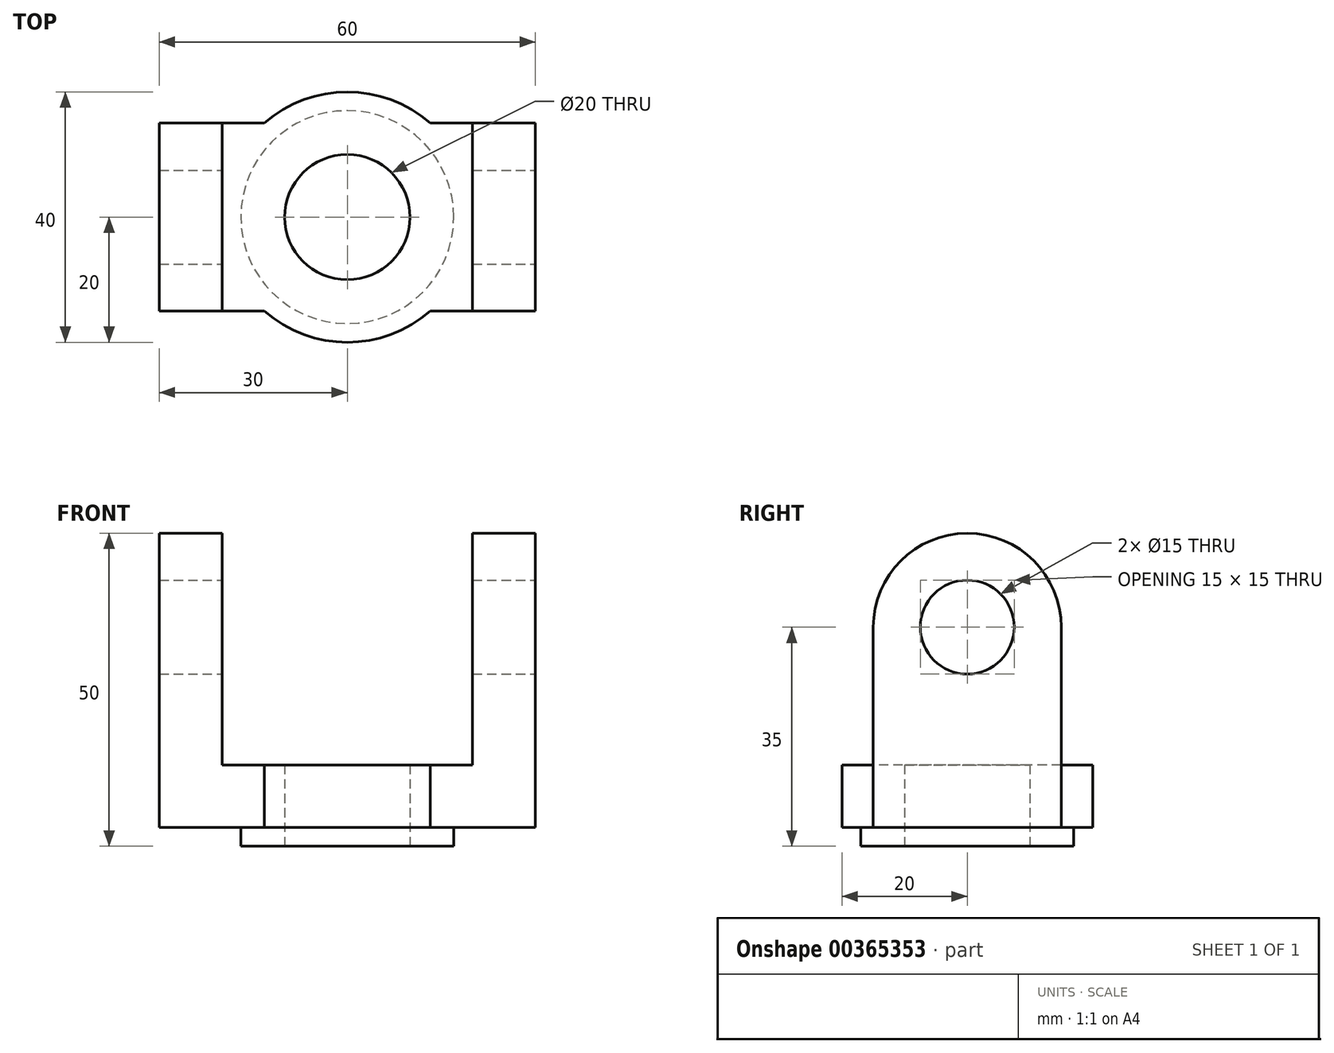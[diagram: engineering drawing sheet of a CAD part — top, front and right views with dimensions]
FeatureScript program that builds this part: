
annotation { "Feature Type Name" : "Feature", "Feature Type Description" : "" }
export const myFeature = defineFeature(function(context is Context, id is Id, definition is map)
    precondition{}
    {
        {
            var Q0;
            Q0=qCreatedBy(makeId("Top.planeOp"),FACE);
            var sketch = newSketch(context, id + "F0", { "sketchPlane" : qUnion([Q0])});
            skArc(sketch, "E0", {"start": v(-13.23, -15) * mm, "mid": v(0, -20) * mm, "end": v(13.23, -15) * mm});
            skLineSegment(sketch, "E1.bottom", {"start": v(-30, 15) * mm, "end": v(30, 15) * mm});
            skLineSegment(sketch, "E1.top", {"start": v(-30, -15) * mm, "end": v(30, -15) * mm});
            skLineSegment(sketch, "E1.left", {"start": v(-30, 15) * mm, "end": v(-30, -15) * mm});
            skLineSegment(sketch, "E1.right", {"start": v(30, 15) * mm, "end": v(30, -15) * mm});
            skCircle(sketch, "E2", {"center": v(0, 0) * mm, "radius": 10 * mm});
            skArc(sketch, "E3.trimOffspring", {"start": v(13.23, 15) * mm, "mid": v(0, 20) * mm, "end": v(-13.23, 15) * mm});
            skSolve(sketch);
        }
        {
            var Q0;
            {var subQ0=sQuery(id+"F0.wireOp",EDGE,"E3.trimOffspring");Q0=makeQuery(id+"F0.imprint","IMPRINT",FACE,{"disambiguationData":[TD([[makeQuery(id+"F0.imprint","IMPRINT",EDGE,{"derivedFrom":subQ0}),1.0]])]});}
            var Q1;
            {var subQ3=sQuery(id+"F0.wireOp",EDGE,"E1.left");Q1=makeQuery(id+"F0.imprint","IMPRINT",FACE,{"disambiguationData":[TD([[makeQuery(id+"F0.imprint","IMPRINT",EDGE,{"derivedFrom":subQ3}),1.0]])]});}
            var Q2;
            {var subQ0=sQuery(id+"F0.wireOp",EDGE,"E0");Q2=makeQuery(id+"F0.imprint","IMPRINT",FACE,{"disambiguationData":[TD([[makeQuery(id+"F0.imprint","IMPRINT",EDGE,{"derivedFrom":subQ0}),1.0]])]});}
            extrude(context, id + "F1", {"entities" : qUnion([Q0, Q1, Q2]), "depth" : 50 * mm});
        }
        {
            var Q0;
            Q0=qCreatedBy(makeId("Front.planeOp"),FACE);
            var sketch = newSketch(context, id + "F2", { "sketchPlane" : qUnion([Q0])});
            skLineSegment(sketch, "E4", {"start": v(17, 0) * mm, "end": v(17, 3) * mm});
            skLineSegment(sketch, "E5", {"start": v(17, 3) * mm, "end": v(30, 3) * mm});
            skLineSegment(sketch, "E6", {"start": v(20, 50) * mm, "end": v(20, 13) * mm});
            skLineSegment(sketch, "E7", {"start": v(-17, 3) * mm, "end": v(-17, 0) * mm});
            skLineSegment(sketch, "E8", {"start": v(-17, 3) * mm, "end": v(-30, 3) * mm});
            skLineSegment(sketch, "E9", {"start": v(-20, 50) * mm, "end": v(-20, 13) * mm});
            skLineSegment(sketch, "E10", {"start": v(-20, 13) * mm, "end": v(20, 13) * mm});
            skLineSegment(sketch, "E11", {"start": v(-20, 50) * mm, "end": v(20, 50) * mm});
            skLineSegment(sketch, "E12", {"start": v(-30, 3) * mm, "end": v(-30, 0) * mm});
            skLineSegment(sketch, "E13", {"start": v(-30, 0) * mm, "end": v(-17, 0) * mm});
            skLineSegment(sketch, "E14", {"start": v(17, 0) * mm, "end": v(30, 0) * mm});
            skLineSegment(sketch, "E15", {"start": v(30, 0) * mm, "end": v(30, 3) * mm});
            skPoint(sketch, "E16.end.orphan", {"position": v(-30, 50) * mm});
            skLineSegment(sketch, "E17", {"start": v(0, 50) * mm, "end": v(0, 13) * mm, "construction": true});
            skSolve(sketch);
        }
        {
            var Q0;
            Q0 = qSketchRegion(id + "F2", true);
            extrude(context, id + "F3", {"entities" : qUnion([Q0]), "operationType" : NewBodyOperationType.REMOVE, "endBound" : BoundingType.SYMMETRIC, "oppositeDirection" : true, "depth" : 75 * mm});
        }
        {
            var Q0;
            Q0=makeQuery(id+"F1.opExtrude","CAP_FACE",FACE,{"disambiguationData":[OSD([sQuery(id+"F0.wireOp",EDGE,"E0"),sQuery(id+"F0.wireOp",EDGE,"E1.bottom"),sQuery(id+"F0.wireOp",EDGE,"E1.top"),sQuery(id+"F0.wireOp",EDGE,"E1.left"),sQuery(id+"F0.wireOp",EDGE,"E1.right"),sQuery(id+"F0.wireOp",EDGE,"E2"),sQuery(id+"F0.wireOp",EDGE,"E3.trimOffspring")])],"isStart":true});
            var sketch = newSketch(context, id + "F4", { "sketchPlane" : qUnion([Q0])});
            skCircle(sketch, "E18", {"center": v(0, 0) * mm, "radius": 17 * mm});
            skSolve(sketch);
        }
        {
            var Q0;
            {var subQ1=sQuery(id+"F0.wireOp",EDGE,"E0");Q0=makeQuery(id+"F4.imprint","IMPRINT",FACE,{"disambiguationData":[TD([[makeQuery(id+"F4.imprint","IMPRINT",EDGE,{"derivedFrom":makeQuery(id+"F1.opExtrude","CAP_EDGE",EDGE,{"disambiguationData":[OSD([subQ1])],"isStart":true})}),-1.0]])]});}
            var Q1;
            {var subQ1=sQuery(id+"F0.wireOp",EDGE,"E3.trimOffspring");Q1=makeQuery(id+"F4.imprint","IMPRINT",FACE,{"disambiguationData":[TD([[makeQuery(id+"F4.imprint","IMPRINT",EDGE,{"derivedFrom":makeQuery(id+"F1.opExtrude","CAP_EDGE",EDGE,{"disambiguationData":[OSD([subQ1])],"isStart":true})}),-1.0]])]});}
            extrude(context, id + "F5", {"entities" : qUnion([Q0, Q1]), "operationType" : NewBodyOperationType.REMOVE, "oppositeDirection" : true, "depth" : 3 * mm});
        }
        {
            var Q0;
            Q0=makeQuery(id+"F1.opExtrude","SWEPT_FACE",FACE,{"disambiguationData":[OSD([sQuery(id+"F0.wireOp",EDGE,"E1.right")])]});
            var sketch = newSketch(context, id + "F6", { "sketchPlane" : qUnion([Q0])});
            skLineSegment(sketch, "E19", {"start": v(0, 3) * mm, "end": v(0, 35) * mm, "construction": true});
            skCircle(sketch, "E20", {"center": v(0, 35) * mm, "radius": 7.5 * mm});
            skCircle(sketch, "E21", {"center": v(0, 35) * mm, "radius": 15 * mm});
            skSolve(sketch);
        }
        {
            var Q0;
            Q0=makeQuery(id+"F6.imprint","IMPRINT",FACE,{"disambiguationData":[TD([[makeQuery(id+"F6.imprint","IMPRINT",EDGE,{"derivedFrom":sQuery(id+"F6.wireOp",EDGE,"E20")}),1.0]])]});
            var Q1;
            {var subQ0=sQuery(id+"F6.wireOp",EDGE,"E21");var subQ1=sQuery(id+"F0.wireOp",EDGE,"E1.right");var subQ2=makeQuery(id+"F1.opExtrude","CAP_EDGE",EDGE,{"disambiguationData":[OSD([subQ1])],"isStart":false});var subQ3=makeQuery(id+"F6.imprint","INTERSECT",VERTEX,{"derivedFrom":[subQ2,subQ0]});Q1=makeQuery(id+"F6.imprint","IMPRINT",FACE,{"disambiguationData":[TD([[makeQuery(id+"F6.imprint","IMPRINT",EDGE,{"disambiguationData":[TD([[subQ3,-1.0]])],"derivedFrom":subQ0}),-1.0]])]});}
            var Q2;
            {var subQ0=sQuery(id+"F6.wireOp",EDGE,"E21");var subQ1=sQuery(id+"F0.wireOp",EDGE,"E1.right");var subQ2=makeQuery(id+"F1.opExtrude","CAP_EDGE",EDGE,{"disambiguationData":[OSD([subQ1])],"isStart":false});var subQ3=makeQuery(id+"F6.imprint","INTERSECT",VERTEX,{"derivedFrom":[subQ2,subQ0]});Q2=makeQuery(id+"F6.imprint","IMPRINT",FACE,{"disambiguationData":[TD([[makeQuery(id+"F6.imprint","IMPRINT",EDGE,{"disambiguationData":[TD([[subQ3,1.0]])],"derivedFrom":subQ0}),-1.0]])]});}
            extrude(context, id + "F7", {"entities" : qUnion([Q0, Q1, Q2]), "operationType" : NewBodyOperationType.REMOVE, "endBound" : BoundingType.THROUGH_ALL, "oppositeDirection" : true, "depth" : 25 * mm});
        }
    });
